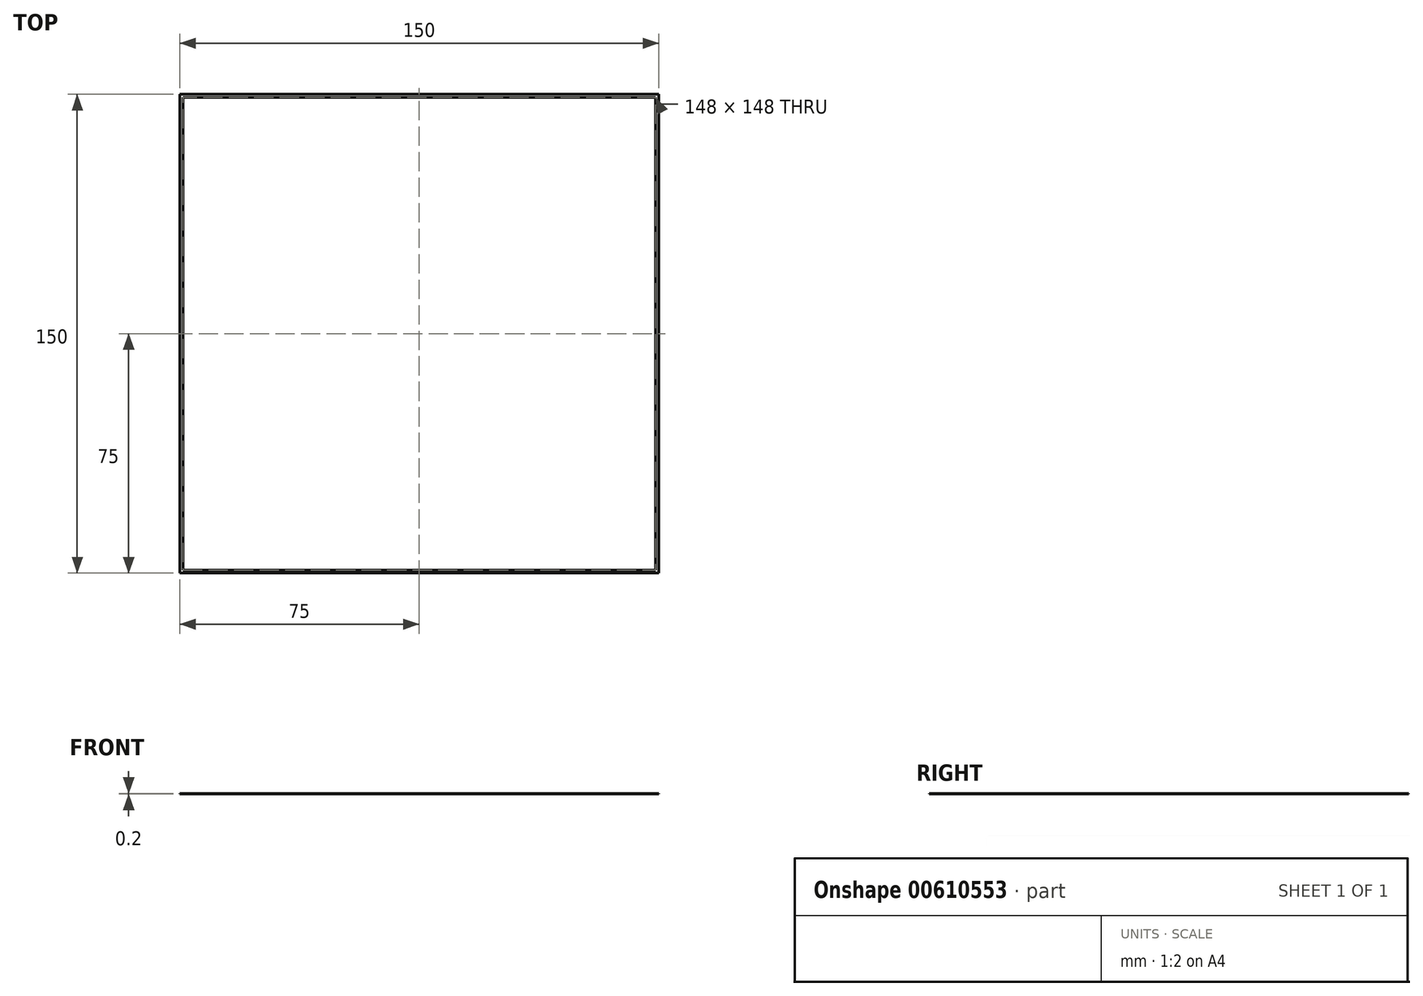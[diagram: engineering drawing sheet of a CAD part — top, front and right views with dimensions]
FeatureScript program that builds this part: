
annotation { "Feature Type Name" : "Feature", "Feature Type Description" : "" }
export const myFeature = defineFeature(function(context is Context, id is Id, definition is map)
    precondition{}
    {
        {
            var Q0;
            Q0=qCreatedBy(makeId("Top.planeOp"),FACE);
            var sketch = newSketch(context, id + "F0", { "sketchPlane" : qUnion([Q0])});
            skLineSegment(sketch, "E0.bottom", {"start": v(75, 75) * mm, "end": v(-75, 75) * mm});
            skLineSegment(sketch, "E0.top", {"start": v(75, -75) * mm, "end": v(-75, -75) * mm});
            skLineSegment(sketch, "E0.left", {"start": v(75, 75) * mm, "end": v(75, -75) * mm});
            skLineSegment(sketch, "E0.right", {"start": v(-75, 75) * mm, "end": v(-75, -75) * mm});
            skPoint(sketch, "E0.middle", {"position": v(0, 0) * mm});
            skLineSegment(sketch, "E1.bottom", {"start": v(74, 74) * mm, "end": v(-74, 74) * mm});
            skLineSegment(sketch, "E1.top", {"start": v(74, -74) * mm, "end": v(-74, -74) * mm});
            skLineSegment(sketch, "E1.left", {"start": v(74, 74) * mm, "end": v(74, -74) * mm});
            skLineSegment(sketch, "E1.right", {"start": v(-74, 74) * mm, "end": v(-74, -74) * mm});
            skSolve(sketch);
        }
        {
            var Q0;
            Q0=makeQuery(id+"F0.imprint","IMPRINT",FACE,{"disambiguationData":[TD([[makeQuery(id+"F0.imprint","IMPRINT",EDGE,{"derivedFrom":sQuery(id+"F0.wireOp",EDGE,"E0.bottom")}),1.0]])]});
            extrude(context, id + "F1", {"entities" : qUnion([Q0]), "depth" : 0.2 * mm, "offsetDistance" : 25 * mm});
        }
    });
